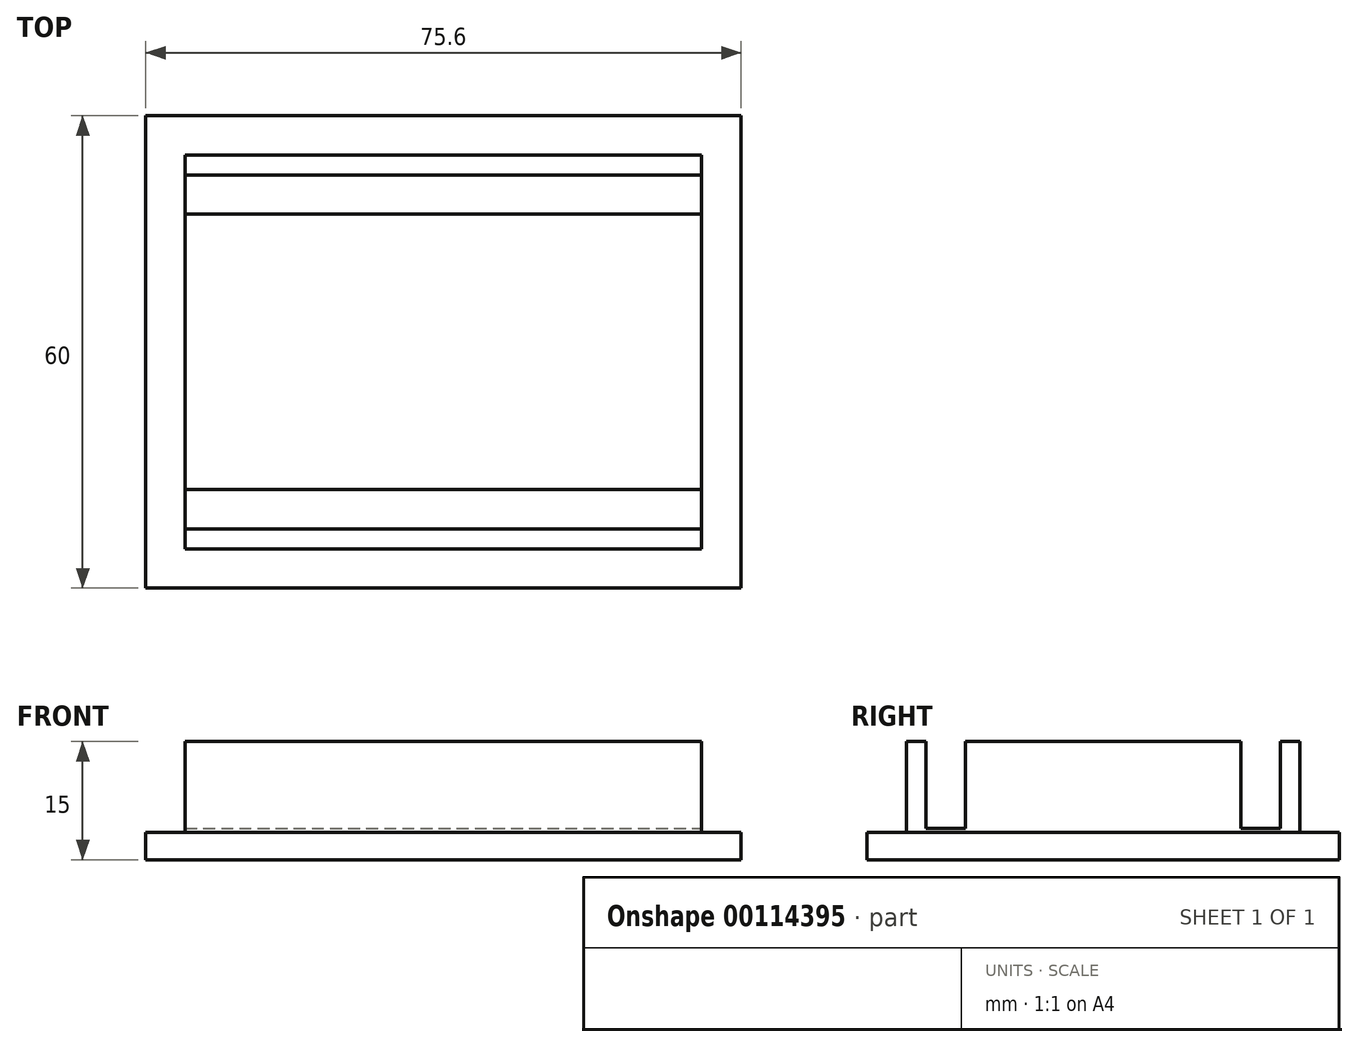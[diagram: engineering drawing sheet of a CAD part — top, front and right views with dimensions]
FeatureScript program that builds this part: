
annotation { "Feature Type Name" : "Feature", "Feature Type Description" : "" }
export const myFeature = defineFeature(function(context is Context, id is Id, definition is map)
    precondition{}
    {
        {
            var Q0;
            Q0=qCreatedBy(makeId("Top.planeOp"),FACE);
            var sketch = newSketch(context, id + "F0", { "sketchPlane" : qUnion([Q0])});
            skLineSegment(sketch, "E0.bottom", {"start": v(0, 0) * mm, "end": v(75.6, 0) * mm});
            skLineSegment(sketch, "E0.top", {"start": v(0, 60) * mm, "end": v(75.6, 60) * mm});
            skLineSegment(sketch, "E0.left", {"start": v(0, 0) * mm, "end": v(0, 60) * mm});
            skLineSegment(sketch, "E0.right", {"start": v(75.6, 0) * mm, "end": v(75.6, 60) * mm});
            skSolve(sketch);
        }
        {
            var Q0;
            Q0=makeQuery(id+"F0.imprint","IMPRINT",FACE,{"disambiguationData":[TD([[makeQuery(id+"F0.imprint","IMPRINT",EDGE,{"derivedFrom":sQuery(id+"F0.wireOp",EDGE,"E0.bottom")}),1.0]])]});
            extrude(context, id + "F1", {"entities" : qUnion([Q0]), "depth" : 3.5 * mm});
        }
        {
            var Q0;
            Q0=makeQuery(id+"F1.opExtrude","CAP_FACE",FACE,{"disambiguationData":[OSD([sQuery(id+"F0.wireOp",EDGE,"E0.bottom"),sQuery(id+"F0.wireOp",EDGE,"E0.top"),sQuery(id+"F0.wireOp",EDGE,"E0.left"),sQuery(id+"F0.wireOp",EDGE,"E0.right")])],"isStart":false});
            var sketch = newSketch(context, id + "F2", { "sketchPlane" : qUnion([Q0])});
            skLineSegment(sketch, "E1.0", {"start": v(5, 55) * mm, "end": v(5, 5) * mm});
            skLineSegment(sketch, "E1.1", {"start": v(70.6, 55) * mm, "end": v(5, 55) * mm});
            skLineSegment(sketch, "E1.2", {"start": v(70.6, 5) * mm, "end": v(70.6, 55) * mm});
            skLineSegment(sketch, "E1.3", {"start": v(5, 5) * mm, "end": v(70.6, 5) * mm});
            skSolve(sketch);
        }
        {
            var Q0;
            Q0=makeQuery(id+"F2.imprint","IMPRINT",FACE,{"disambiguationData":[TD([[makeQuery(id+"F2.imprint","IMPRINT",EDGE,{"derivedFrom":sQuery(id+"F2.wireOp",EDGE,"E1.0")}),1.0]])]});
            extrude(context, id + "F3", {"entities" : qUnion([Q0]), "operationType" : NewBodyOperationType.ADD, "depth" : 11.5 * mm});
        }
        {
            var Q0;
            Q0=makeQuery(id+"F3.opExtrude","CAP_FACE",FACE,{"disambiguationData":[OSD([sQuery(id+"F2.wireOp",EDGE,"E1.0"),sQuery(id+"F2.wireOp",EDGE,"E1.1"),sQuery(id+"F2.wireOp",EDGE,"E1.2"),sQuery(id+"F2.wireOp",EDGE,"E1.3")])],"isStart":false});
            var sketch = newSketch(context, id + "F4", { "sketchPlane" : qUnion([Q0])});
            skLineSegment(sketch, "E2.bottom", {"start": v(5, 12.5) * mm, "end": v(70.6, 12.5) * mm});
            skLineSegment(sketch, "E2.top", {"start": v(5, 7.5) * mm, "end": v(70.6, 7.5) * mm});
            skLineSegment(sketch, "E2.left", {"start": v(5, 12.5) * mm, "end": v(5, 7.5) * mm});
            skLineSegment(sketch, "E2.right", {"start": v(70.6, 12.5) * mm, "end": v(70.6, 7.5) * mm});
            skLineSegment(sketch, "E3", {"start": v(5, 30) * mm, "end": v(70.6, 30) * mm, "construction": true});
            skLineSegment(sketch, "E4.MirrorCS", {"start": v(70.6, 47.5) * mm, "end": v(70.6, 52.5) * mm});
            skLineSegment(sketch, "E5.MirrorCS", {"start": v(5, 47.5) * mm, "end": v(5, 52.5) * mm});
            skLineSegment(sketch, "E6.MirrorCS", {"start": v(5, 52.5) * mm, "end": v(70.6, 52.5) * mm});
            skLineSegment(sketch, "E7.MirrorCS", {"start": v(5, 47.5) * mm, "end": v(70.6, 47.5) * mm});
            skSolve(sketch);
        }
        {
            var Q0;
            Q0=makeQuery(id+"F4.imprint","IMPRINT",FACE,{"disambiguationData":[TD([[makeQuery(id+"F4.imprint","IMPRINT",EDGE,{"derivedFrom":sQuery(id+"F4.wireOp",EDGE,"E4.MirrorCS")}),1.0]])]});
            var Q1;
            Q1=makeQuery(id+"F4.imprint","IMPRINT",FACE,{"disambiguationData":[TD([[makeQuery(id+"F4.imprint","IMPRINT",EDGE,{"derivedFrom":sQuery(id+"F4.wireOp",EDGE,"E2.bottom")}),-1.0]])]});
            extrude(context, id + "F5", {"entities" : qUnion([Q0, Q1]), "operationType" : NewBodyOperationType.REMOVE, "oppositeDirection" : true, "depth" : 11 * mm});
        }
    });
